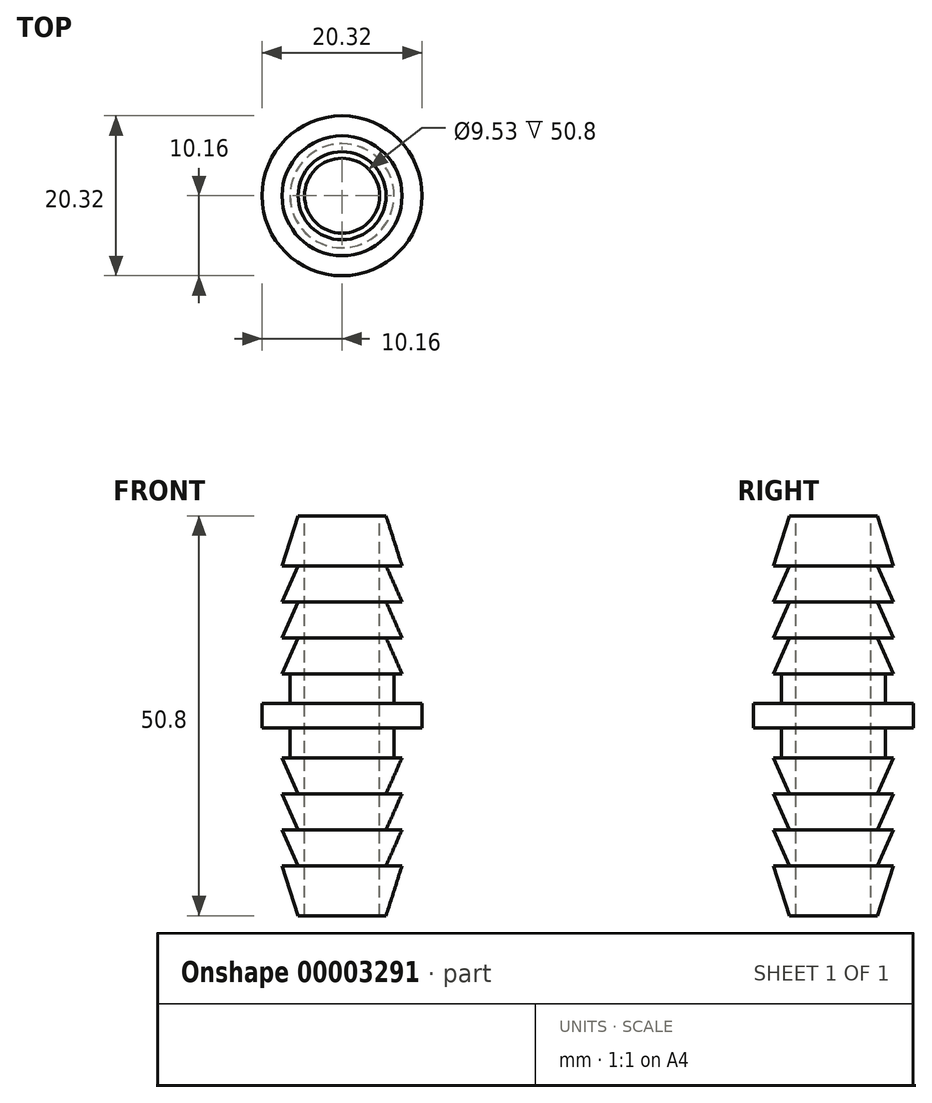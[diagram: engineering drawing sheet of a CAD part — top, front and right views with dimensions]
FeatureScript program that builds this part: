
annotation { "Feature Type Name" : "Feature", "Feature Type Description" : "" }
export const myFeature = defineFeature(function(context is Context, id is Id, definition is map)
    precondition{}
    {
        {
            var Q0;
            Q0=qCreatedBy(makeId("Front.planeOp"),FACE);
            var sketch = newSketch(context, id + "F0", { "sketchPlane" : qUnion([Q0])});
            skLineSegment(sketch, "E0", {"start": v(0, 0) * mm, "end": v(5.59, 0) * mm});
            skLineSegment(sketch, "E1", {"start": v(0, 25.4) * mm, "end": v(0, 0) * mm});
            skLineSegment(sketch, "E2", {"start": v(7.62, 6.35) * mm, "end": v(5.59, 0) * mm});
            skLineSegment(sketch, "E3", {"start": v(5.59, 0) * mm, "end": v(5.59, 25.4) * mm, "construction": true});
            skLineSegment(sketch, "E4", {"start": v(7.62, 6.35) * mm, "end": v(5.59, 6.35) * mm});
            skLineSegment(sketch, "E5", {"start": v(5.59, 6.35) * mm, "end": v(7.62, 10.92) * mm});
            skLineSegment(sketch, "E6", {"start": v(7.62, 10.92) * mm, "end": v(5.59, 10.92) * mm});
            skLineSegment(sketch, "E7", {"start": v(5.59, 10.92) * mm, "end": v(7.62, 15.5) * mm});
            skLineSegment(sketch, "E8", {"start": v(7.62, 15.5) * mm, "end": v(5.59, 15.5) * mm});
            skLineSegment(sketch, "E9", {"start": v(5.59, 15.5) * mm, "end": v(7.62, 20.07) * mm});
            skLineSegment(sketch, "E10", {"start": v(7.62, 20.07) * mm, "end": v(5.59, 20.07) * mm});
            skLineSegment(sketch, "E11", {"start": v(7.62, 25.4) * mm, "end": v(7.62, 25.4) * mm});
            skLineSegment(sketch, "E12", {"start": v(6.6, 23.87) * mm, "end": v(10.16, 23.87) * mm});
            skLineSegment(sketch, "E13", {"start": v(10.16, 23.87) * mm, "end": v(10.16, 25.39) * mm});
            skLineSegment(sketch, "E14.trimOffspring", {"start": v(7.62, 23.87) * mm, "end": v(7.62, 23.81) * mm});
            skPoint(sketch, "E15.orphan", {"position": v(7.62, 0) * mm});
            skLineSegment(sketch, "E16", {"start": v(6.6, 20.07) * mm, "end": v(6.6, 23.87) * mm});
            skLineSegment(sketch, "E17", {"start": v(0, 25.4) * mm, "end": v(0, 50.8) * mm});
            skLineSegment(sketch, "E18", {"start": v(0, 50.8) * mm, "end": v(5.59, 50.8) * mm});
            skLineSegment(sketch, "E19", {"start": v(10.16, 26.98) * mm, "end": v(10.16, 25.39) * mm});
            skLineSegment(sketch, "E20", {"start": v(5.59, 25.4) * mm, "end": v(5.59, 50.8) * mm, "construction": true});
            skLineSegment(sketch, "E21", {"start": v(5.59, 50.8) * mm, "end": v(7.62, 44.45) * mm});
            skLineSegment(sketch, "E22", {"start": v(7.62, 44.45) * mm, "end": v(5.59, 44.45) * mm});
            skLineSegment(sketch, "E23", {"start": v(5.59, 44.45) * mm, "end": v(7.62, 39.88) * mm});
            skLineSegment(sketch, "E24", {"start": v(7.62, 39.88) * mm, "end": v(5.59, 39.88) * mm});
            skLineSegment(sketch, "E25", {"start": v(5.59, 39.88) * mm, "end": v(7.62, 35.3) * mm});
            skLineSegment(sketch, "E26", {"start": v(7.62, 35.3) * mm, "end": v(5.59, 35.3) * mm});
            skLineSegment(sketch, "E27", {"start": v(5.59, 35.3) * mm, "end": v(7.62, 30.73) * mm});
            skLineSegment(sketch, "E28", {"start": v(7.62, 30.73) * mm, "end": v(5.59, 30.73) * mm});
            skLineSegment(sketch, "E29", {"start": v(6.6, 25.4) * mm, "end": v(6.6, 25.4) * mm});
            skLineSegment(sketch, "E30.trimOffspring", {"start": v(6.6, 26.98) * mm, "end": v(6.61, 30.73) * mm});
            skLineSegment(sketch, "E31.trimOffspring", {"start": v(7.62, 26.98) * mm, "end": v(10.16, 26.98) * mm});
            skLineSegment(sketch, "E32.trimOffspring", {"start": v(7.62, 30.73) * mm, "end": v(7.62, 26.98) * mm});
            skLineSegment(sketch, "E33", {"start": v(7.62, 26.98) * mm, "end": v(6.6, 26.98) * mm});
            skPoint(sketch, "E34.orphan", {"position": v(7.62, 50.8) * mm});
            skSolve(sketch);
        }
        {
            var Q0;
            Q0=makeQuery(id+"F0.imprint","IMPRINT",FACE,{"disambiguationData":[TD([[makeQuery(id+"F0.imprint","IMPRINT",EDGE,{"derivedFrom":sQuery(id+"F0.wireOp",EDGE,"E0")}),1.0]])]});
            var Q1;
            Q1=sQuery(id+"F0.wireOp",EDGE,"E1");
            revolve(context, id + "F1", {"entities" : qUnion([Q0]), "axis" : qUnion([Q1]), "revolveType" : RevolveType.FULL});
        }
        {
            var Q0;
            Q0=makeQuery(id+"F1.opRevolve","SWEPT_FACE",FACE,{"disambiguationData":[OSD([sQuery(id+"F0.wireOp",EDGE,"E18")])]});
            var sketch = newSketch(context, id + "F2", { "sketchPlane" : qUnion([Q0])});
            skCircle(sketch, "E35", {"center": v(0, 0) * mm, "radius": 4.76 * mm});
            skSolve(sketch);
        }
        {
            var Q0;
            Q0=makeQuery(id+"F2.imprint","IMPRINT",FACE,{"disambiguationData":[TD([[makeQuery(id+"F2.imprint","IMPRINT",EDGE,{"derivedFrom":sQuery(id+"F2.wireOp",EDGE,"E35")}),1.0]])]});
            extrude(context, id + "F3", {"entities" : qUnion([Q0]), "operationType" : NewBodyOperationType.REMOVE, "endBound" : BoundingType.THROUGH_ALL, "oppositeDirection" : true, "depth" : 25.4 * mm});
        }
    });
